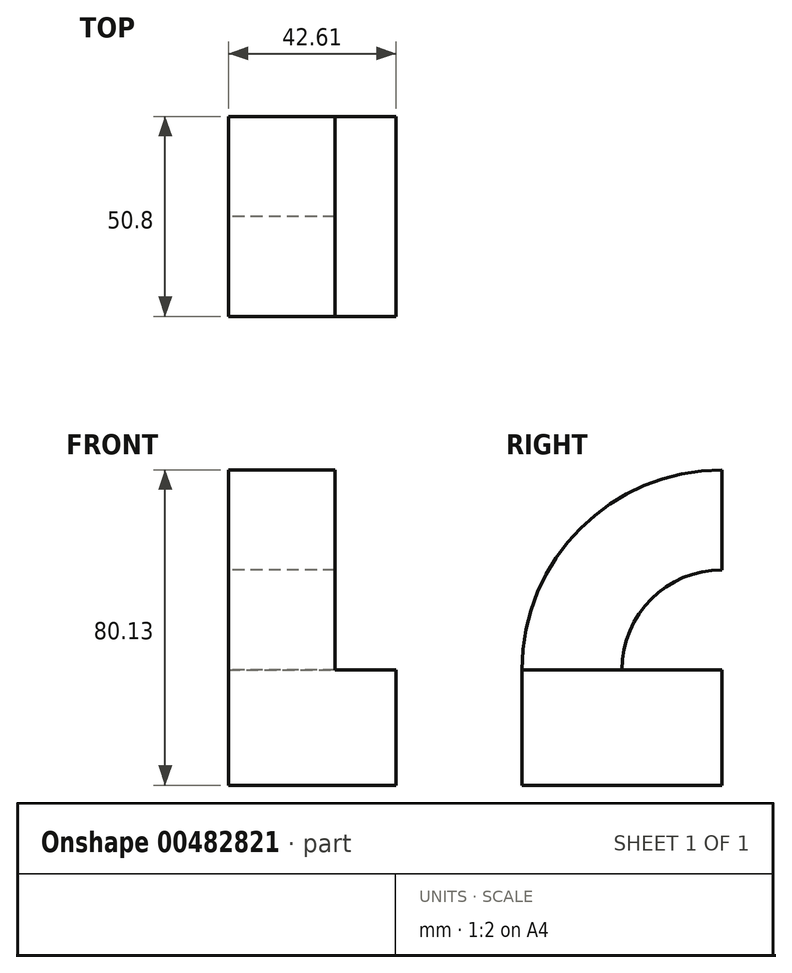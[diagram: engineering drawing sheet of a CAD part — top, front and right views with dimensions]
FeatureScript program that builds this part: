
annotation { "Feature Type Name" : "Feature", "Feature Type Description" : "" }
export const myFeature = defineFeature(function(context is Context, id is Id, definition is map)
    precondition{}
    {
        {
            var Q0;
            Q0=qCreatedBy(makeId("Front.planeOp"),FACE);
            var sketch = newSketch(context, id + "F0", { "sketchPlane" : qUnion([Q0])});
            skLineSegment(sketch, "E0.bottom", {"start": v(-42.61, 29.33) * mm, "end": v(0, 29.33) * mm});
            skLineSegment(sketch, "E0.top", {"start": v(-42.61, 0) * mm, "end": v(0, 0) * mm});
            skLineSegment(sketch, "E0.left", {"start": v(-42.61, 29.33) * mm, "end": v(-42.61, 0) * mm});
            skLineSegment(sketch, "E0.right", {"start": v(0, 29.33) * mm, "end": v(0, 0) * mm});
            skSolve(sketch);
        }
        {
            var Q0;
            Q0 = qSketchRegion(id + "F0", true);
            extrude(context, id + "F1", {"entities" : qUnion([Q0]), "endBound" : BoundingType.SYMMETRIC, "depth" : 50.8 * mm});
        }
        {
            var Q0;
            Q0=makeQuery(id+"F1.opExtrude","SWEPT_FACE",FACE,{"disambiguationData":[OSD([sQuery(id+"F0.wireOp",EDGE,"E0.bottom")])]});
            var sketch = newSketch(context, id + "F2", { "sketchPlane" : qUnion([Q0])});
            skLineSegment(sketch, "E1.bottom", {"start": v(-15.5, -25.4) * mm, "end": v(-42.61, -25.4) * mm});
            skLineSegment(sketch, "E1.top", {"start": v(-15.5, 0) * mm, "end": v(-42.61, 0) * mm});
            skLineSegment(sketch, "E1.left", {"start": v(-15.5, -25.4) * mm, "end": v(-15.5, 0) * mm});
            skLineSegment(sketch, "E1.right", {"start": v(-42.61, -25.4) * mm, "end": v(-42.61, 0) * mm});
            skSolve(sketch);
        }
        {
            var Q0;
            Q0 = qSketchRegion(id + "F2", true);
            var Q1;
            Q1=makeQuery(id+"F1.opExtrude","CAP_EDGE",EDGE,{"disambiguationData":[OSD([sQuery(id+"F0.wireOp",EDGE,"E0.bottom")])],"isStart":true});
            revolve(context, id + "F3", {"operationType" : NewBodyOperationType.ADD, "entities" : qUnion([Q0]), "axis" : qUnion([Q1]), "revolveType" : RevolveType.ONE_DIRECTION, "oppositeDirection" : true, "angle" : 90 * degree});
        }
    });
